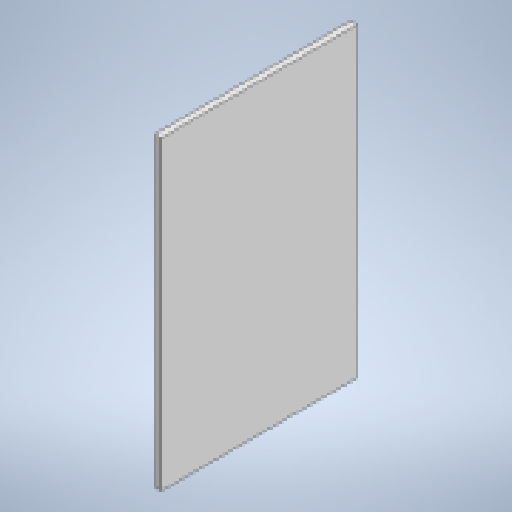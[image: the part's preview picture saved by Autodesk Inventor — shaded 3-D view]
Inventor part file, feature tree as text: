
AUTODESK INVENTOR PART (.ipt)
format: ipt  version: 2023 (Build 270158000, 158)  size: 137,216 bytes
history: native  units: in
note: dims shown in document units (in); Inventor stores cm internally (conversion verified against a paired STEP export)
features: extrude x2, sketch x2
ambient origin geometry x8: Origin, YZ Plane, XZ Plane, XY Plane, X Axis, Y Axis, Z Axis, Center Point
bodies: Solid1 (feature_tree)
feature tree (4):
  extrude  "Extrusion1"  Depth=9.3622in
  extrude  "Extrusion2"  Depth=0.2in
  sketch  "Sketch1"  dims[d0=6.0in d1=9.3622in]
  sketch  "Sketch2"  dims[d2=0.2in d3=0.0in d4=0.315in d5=1.811in d6=0.9843in d7=0.3937in d8=0.2in d9=0.0in]
